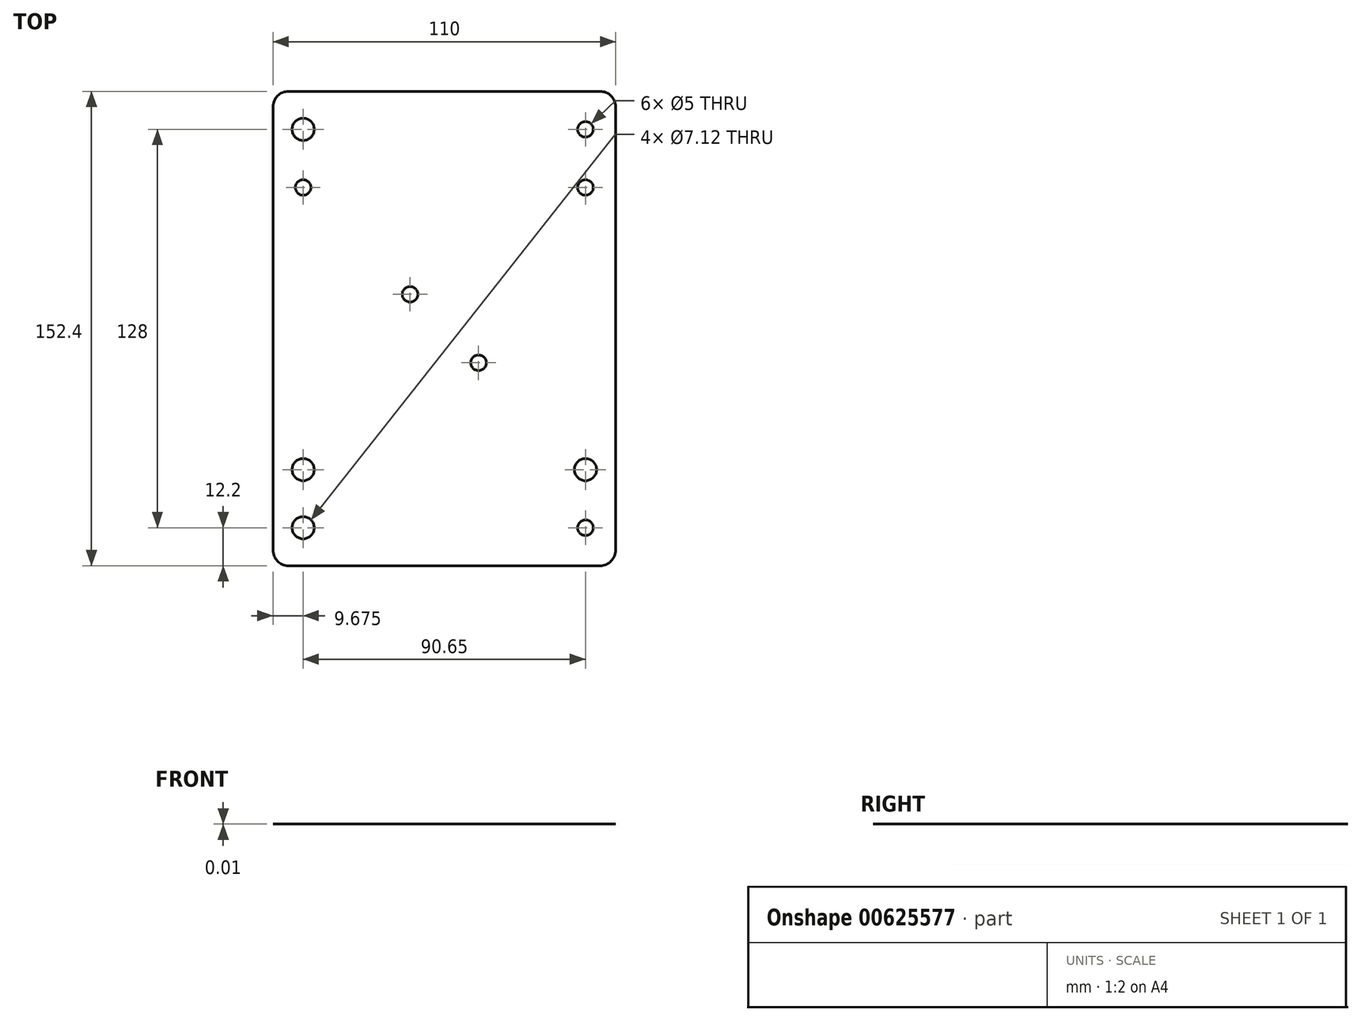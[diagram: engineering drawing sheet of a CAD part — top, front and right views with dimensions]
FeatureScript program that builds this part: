
annotation { "Feature Type Name" : "Feature", "Feature Type Description" : "" }
export const myFeature = defineFeature(function(context is Context, id is Id, definition is map)
    precondition{}
    {
        {
            var Q0;
            Q0=qCreatedBy(makeId("Top.planeOp"),FACE);
            var sketch = newSketch(context, id + "F0", { "sketchPlane" : qUnion([Q0])});
            skCircle(sketch, "E0", {"center": v(-11, 11) * mm, "radius": 2.5 * mm});
            skCircle(sketch, "E1", {"center": v(-45.32, 45.33) * mm, "radius": 2.5 * mm});
            skCircle(sketch, "E2", {"center": v(-45.32, -45.32) * mm, "radius": 3.56 * mm});
            skCircle(sketch, "E3", {"center": v(45.32, 64) * mm, "radius": 2.5 * mm});
            skCircle(sketch, "E4", {"center": v(-45.33, 64) * mm, "radius": 3.56 * mm});
            skCircle(sketch, "E5", {"center": v(-45.32, -64) * mm, "radius": 3.56 * mm});
            skCircle(sketch, "E6", {"center": v(45.33, -64) * mm, "radius": 2.5 * mm});
            skCircle(sketch, "E7", {"center": v(45.33, -45.32) * mm, "radius": 3.56 * mm});
            skCircle(sketch, "E8", {"center": v(45.32, 45.33) * mm, "radius": 2.5 * mm});
            skCircle(sketch, "E9", {"center": v(11, -11) * mm, "radius": 2.5 * mm});
            skLineSegment(sketch, "E10", {"start": v(-45.33, 64) * mm, "end": v(-45.33, 45.33) * mm, "construction": true});
            skLineSegment(sketch, "E11", {"start": v(-45.32, -45.32) * mm, "end": v(-45.32, 45.33) * mm, "construction": true});
            skLineSegment(sketch, "E12", {"start": v(-45.32, -45.32) * mm, "end": v(-45.32, -64) * mm, "construction": true});
            skLineSegment(sketch, "E13", {"start": v(-45.32, -64) * mm, "end": v(-45.32, -76.2) * mm, "construction": true});
            skLineSegment(sketch, "E14", {"start": v(-45.33, 64) * mm, "end": v(-45.33, 76.2) * mm, "construction": true});
            skLineSegment(sketch, "E15", {"start": v(45.33, 45.33) * mm, "end": v(45.33, -45.32) * mm, "construction": true});
            skLineSegment(sketch, "E16", {"start": v(45.33, -64) * mm, "end": v(45.33, -45.32) * mm, "construction": true});
            skLineSegment(sketch, "E17", {"start": v(45.33, -64) * mm, "end": v(45.33, -76.2) * mm, "construction": true});
            skLineSegment(sketch, "E18", {"start": v(-45.32, -64) * mm, "end": v(45.33, -64) * mm, "construction": true});
            skLineSegment(sketch, "E19", {"start": v(45.33, -64) * mm, "end": v(55, -64) * mm, "construction": true});
            skLineSegment(sketch, "E20", {"start": v(-45.32, -64) * mm, "end": v(-55, -64) * mm, "construction": true});
            skLineSegment(sketch, "E21", {"start": v(-45.32, -45.33) * mm, "end": v(-55, -45.33) * mm, "construction": true});
            skLineSegment(sketch, "E22", {"start": v(-45.32, -45.32) * mm, "end": v(45.33, -45.32) * mm, "construction": true});
            skLineSegment(sketch, "E23", {"start": v(45.33, -45.32) * mm, "end": v(55, -45.32) * mm, "construction": true});
            skLineSegment(sketch, "E24", {"start": v(11, -11) * mm, "end": v(55, -11) * mm, "construction": true});
            skLineSegment(sketch, "E25", {"start": v(11, -11) * mm, "end": v(-55, -11) * mm, "construction": true});
            skLineSegment(sketch, "E26", {"start": v(-11, 11) * mm, "end": v(55, 11) * mm, "construction": true});
            skLineSegment(sketch, "E27", {"start": v(-11, 11) * mm, "end": v(-55, 11) * mm, "construction": true});
            skLineSegment(sketch, "E28", {"start": v(-45.32, 45.33) * mm, "end": v(45.32, 45.33) * mm, "construction": true});
            skLineSegment(sketch, "E29", {"start": v(45.32, 45.33) * mm, "end": v(55, 45.33) * mm, "construction": true});
            skLineSegment(sketch, "E30", {"start": v(-45.32, 45.33) * mm, "end": v(-55, 45.33) * mm, "construction": true});
            skLineSegment(sketch, "E31", {"start": v(-45.33, 64) * mm, "end": v(45.32, 64) * mm, "construction": true});
            skLineSegment(sketch, "E32", {"start": v(45.32, 64) * mm, "end": v(55, 64) * mm, "construction": true});
            skLineSegment(sketch, "E33", {"start": v(-45.33, 64) * mm, "end": v(-55, 64) * mm, "construction": true});
            skLineSegment(sketch, "E34", {"start": v(-11, 11) * mm, "end": v(-11, 76.2) * mm, "construction": true});
            skLineSegment(sketch, "E35", {"start": v(-11, 11) * mm, "end": v(-11, -76.2) * mm, "construction": true});
            skLineSegment(sketch, "E36", {"start": v(11, -11) * mm, "end": v(11, -76.2) * mm, "construction": true});
            skLineSegment(sketch, "E37", {"start": v(11, -11) * mm, "end": v(11, 76.2) * mm, "construction": true});
            skLineSegment(sketch, "E38", {"start": v(-11, 11) * mm, "end": v(11, -11) * mm, "construction": true});
            skPoint(sketch, "E39", {"position": v(0, 0) * mm});
            skLineSegment(sketch, "E40", {"start": v(45.32, 64) * mm, "end": v(45.32, 76.2) * mm, "construction": true});
            skLineSegment(sketch, "E41", {"start": v(45.32, 64) * mm, "end": v(45.32, 45.33) * mm, "construction": true});
            skLineSegment(sketch, "E42.bottom", {"start": v(-55, 76.2) * mm, "end": v(55, 76.2) * mm});
            skLineSegment(sketch, "E42.top", {"start": v(-55, -76.2) * mm, "end": v(55, -76.2) * mm});
            skLineSegment(sketch, "E42.left", {"start": v(-55, 76.2) * mm, "end": v(-55, -76.2) * mm});
            skLineSegment(sketch, "E42.right", {"start": v(55, 76.2) * mm, "end": v(55, -76.2) * mm});
            skLineSegment(sketch, "E43", {"start": v(-55, 0) * mm, "end": v(55, 0) * mm, "construction": true});
            skLineSegment(sketch, "E44", {"start": v(0, 76.2) * mm, "end": v(0, -76.2) * mm, "construction": true});
            skSolve(sketch);
        }
        {
            var Q0;
            Q0 = qSketchRegion(id + "F0", true);
            extrude(context, id + "F1", {"entities" : qUnion([Q0]), "depth" : 1 / 101.6 * mm, "offsetDistance" : 25 * mm});
        }
        {
            var Q0;
            Q0=makeQuery(id+"F1.opExtrude","SWEPT_EDGE",EDGE,{"disambiguationData":[OSD([sQuery(id+"F0.wireOp",EDGE,"E42.bottom"),sQuery(id+"F0.wireOp",EDGE,"E42.left")])]});
            var Q1;
            Q1=makeQuery(id+"F1.opExtrude","SWEPT_EDGE",EDGE,{"disambiguationData":[OSD([sQuery(id+"F0.wireOp",EDGE,"E42.bottom"),sQuery(id+"F0.wireOp",EDGE,"E42.right")])]});
            var Q2;
            Q2=makeQuery(id+"F1.opExtrude","SWEPT_EDGE",EDGE,{"disambiguationData":[OSD([sQuery(id+"F0.wireOp",EDGE,"E42.top"),sQuery(id+"F0.wireOp",EDGE,"E42.right")])]});
            var Q3;
            Q3=makeQuery(id+"F1.opExtrude","SWEPT_EDGE",EDGE,{"disambiguationData":[OSD([sQuery(id+"F0.wireOp",EDGE,"E42.top"),sQuery(id+"F0.wireOp",EDGE,"E42.left")])]});
            fillet(context, id + "F2", {"entities" : qUnion([Q0, Q1, Q2, Q3]), "radius" : 5 * mm, "tangentPropagation" : true, "allowEdgeOverflow" : false});
        }
    });
